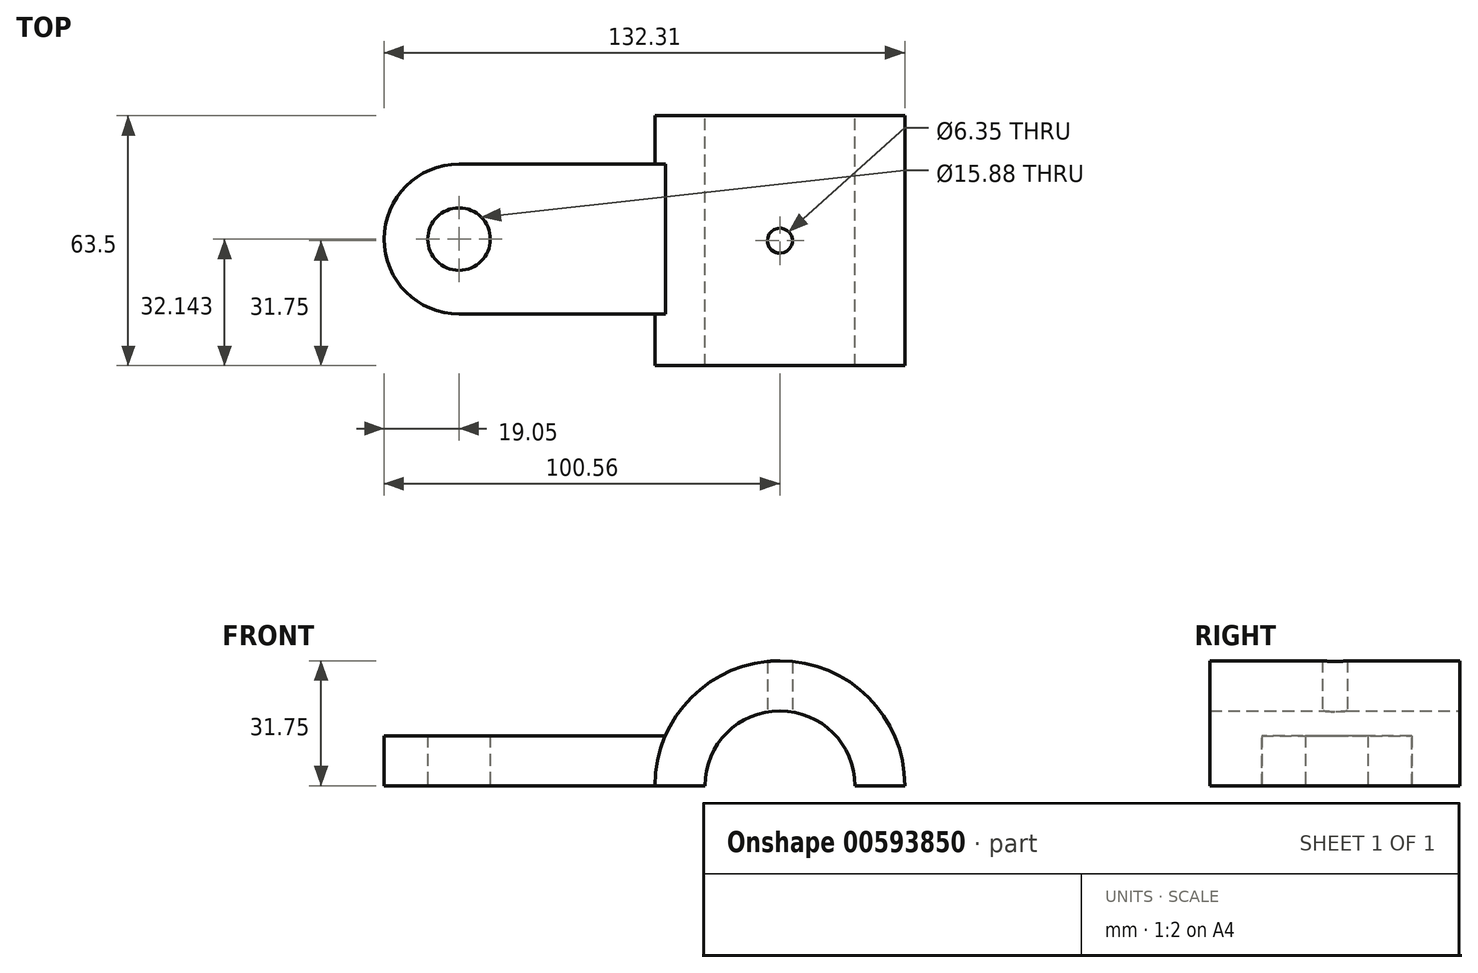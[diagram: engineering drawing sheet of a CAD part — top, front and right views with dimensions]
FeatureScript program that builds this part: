
annotation { "Feature Type Name" : "Feature", "Feature Type Description" : "" }
export const myFeature = defineFeature(function(context is Context, id is Id, definition is map)
    precondition{}
    {
        {
            var Q0;
            Q0=qCreatedBy(makeId("Front.planeOp"),FACE);
            var sketch = newSketch(context, id + "F0", { "sketchPlane" : qUnion([Q0])});
            skArc(sketch, "E0", {"start": v(-19.05, 0) * mm, "mid": v(0, 19.05) * mm, "end": v(19.05, 0) * mm});
            skArc(sketch, "E1", {"start": v(-31.75, 0) * mm, "mid": v(0, 31.75) * mm, "end": v(31.75, 0) * mm});
            skLineSegment(sketch, "E2", {"start": v(31.75, 0) * mm, "end": v(19.05, 0) * mm});
            skLineSegment(sketch, "E3", {"start": v(-19.05, 0) * mm, "end": v(-31.75, 0) * mm});
            skSolve(sketch);
        }
        {
            var Q0;
            Q0 = qSketchRegion(id + "F0", true);
            extrude(context, id + "F1", {"entities" : qUnion([Q0]), "endBound" : BoundingType.SYMMETRIC, "depth" : 63.5 * mm, "offsetDistance" : 25.4 * mm});
        }
        {
            var Q0;
            Q0=qCreatedBy(makeId("Top.planeOp"),FACE);
            var sketch = newSketch(context, id + "F2", { "sketchPlane" : qUnion([Q0])});
            skCircle(sketch, "E4", {"center": v(0, 0) * mm, "radius": 3.17 * mm});
            skArc(sketch, "E5", {"start": v(82.51, 19.02) * mm, "mid": v(101.56, -0.03) * mm, "end": v(82.51, -19.08) * mm});
            skArc(sketch, "E6", {"start": v(-81.5, 19.44) * mm, "mid": v(-100.56, 0.4) * mm, "end": v(-81.5, -18.66) * mm});
            skCircle(sketch, "E7", {"center": v(-81.5, 0.4) * mm, "radius": 7.94 * mm});
            skCircle(sketch, "E8", {"center": v(82.51, -0.03) * mm, "radius": 7.94 * mm});
            skLineSegment(sketch, "E9.0", {"start": v(-19.05, -31.75) * mm, "end": v(-19.05, 31.75) * mm});
            skLineSegment(sketch, "E10.0", {"start": v(19.05, -31.75) * mm, "end": v(19.05, 31.75) * mm});
            skLineSegment(sketch, "E11", {"start": v(-81.5, 19.44) * mm, "end": v(-19.05, 19.44) * mm});
            skLineSegment(sketch, "E12", {"start": v(-81.5, -18.66) * mm, "end": v(-19.05, -18.66) * mm});
            skLineSegment(sketch, "E13", {"start": v(82.51, 19.02) * mm, "end": v(19.05, 19.02) * mm});
            skLineSegment(sketch, "E14", {"start": v(82.51, -19.08) * mm, "end": v(19.05, -19.08) * mm});
            skSolve(sketch);
        }
        {
            var Q0;
            Q0=makeQuery(id+"F2.imprint","IMPRINT",FACE,{"disambiguationData":[TD([[makeQuery(id+"F2.imprint","IMPRINT",EDGE,{"derivedFrom":sQuery(id+"F2.wireOp",EDGE,"E4")}),1.0]])]});
            extrude(context, id + "F3", {"entities" : qUnion([Q0]), "operationType" : NewBodyOperationType.REMOVE, "depth" : 41.4 * mm, "offsetDistance" : 25.4 * mm});
        }
        {
            var Q0;
            Q0=makeQuery(id+"F2.imprint","IMPRINT",FACE,{"disambiguationData":[TD([[makeQuery(id+"F2.imprint","IMPRINT",EDGE,{"derivedFrom":sQuery(id+"F2.wireOp",EDGE,"E5")}),-1.0]])]});
            var Q1;
            Q1=makeQuery(id+"F2.imprint","IMPRINT",FACE,{"disambiguationData":[TD([[makeQuery(id+"F2.imprint","IMPRINT",EDGE,{"derivedFrom":sQuery(id+"F2.wireOp",EDGE,"E6")}),1.0]])]});
            extrude(context, id + "F4", {"entities" : qUnion([Q0, Q1]), "operationType" : NewBodyOperationType.ADD, "depth" : 12.7 * mm, "offsetDistance" : 25.4 * mm});
        }
    });
